# Revit family: Furniture_Other_Sjobergs_Cutting_Table
name_source: partatom
category: Furniture
revit_build: Autodesk Revit 2017 (Build: 20190508_0315(x64)
units: mm (PartAtom-declared; Revit-internal decimal feet)

## family parameters
Always vertical = Yes
Cut with Voids When Loaded = No
OmniClass Number = 23.40.20.27.21
OmniClass Title = Mobile Storage Units
Room Calculation Point = No
Shared = No
Work Plane-Based = No

## types (1)
- Cutting Table
    AssetType = Movable
    BIMObjectName = Furniture_Other_Sjobergs_Cutting_Table
    Brand = Sjobergs
    Category = Cutting Table
    Color = Various
    Constituents = Paper roll holder 33115, Tilt drawer 33112, Drawers 33229, Flap 33118
    ConvergoRefNr = 0184-2005-0009-SE
    Cost = 0 $
    CuttingTableTertiaryMaterial = Grey laminate
    Features = The table can be equipped with various accessories, such as the flap, the drawer set and the rocker box.
    IfcExportAs = IfcFurnitureType
    IfcExportType = DRAWER
    MainColor = Wooden
    ManufacterURL = https://www.sjobergs.se
    Manufacturer = Sjöbergs
    ManufacturerName = Sjöbergs
    Material = Wood & Metal
    Model = Cutting Table
    ModelNumber = 33061
    NBSDescription = School art, design and technology tables and workbenches;
    NBSReference = 45-35-20/320
    Name = Sjobergs_Cutting_Table
    NominalDepth = 936 mm  [stored 3.07087 ft]
    NominalHeight = 897 mm
    NominalWidth = 1700 mm  [stored 5.57743 ft]
    ProductDatasheet = https://www.sjobergs.se
    ProductInformation = A complete table consists of slab 33108 in dark warped laminate. Tripod 33111 in book. A flap 33118, a box set 33229 and a tipping box 33112 in dark warped laminate.
    Shape = Rectangular
    Size = 600 x1200 x 897 mm
    URL = https://www.sjobergs.se
    Uniclass2 = Pr_40_50_21
    Uniclass2015Description = Desks, Tables And Worktops
    Uniclass2015Reference = Pr_40_50_21_76
    Version = 1
    VersionDate = 30/06/2020
    Weight = 97,7 kg

note: [stored X ft] marks values corroborated as IEEE doubles in the binary element streams (Revit-internal decimal feet)

## geometry (parser evidence)
native form markers: Sweep x7
no freeform markers — native parametric forms only
